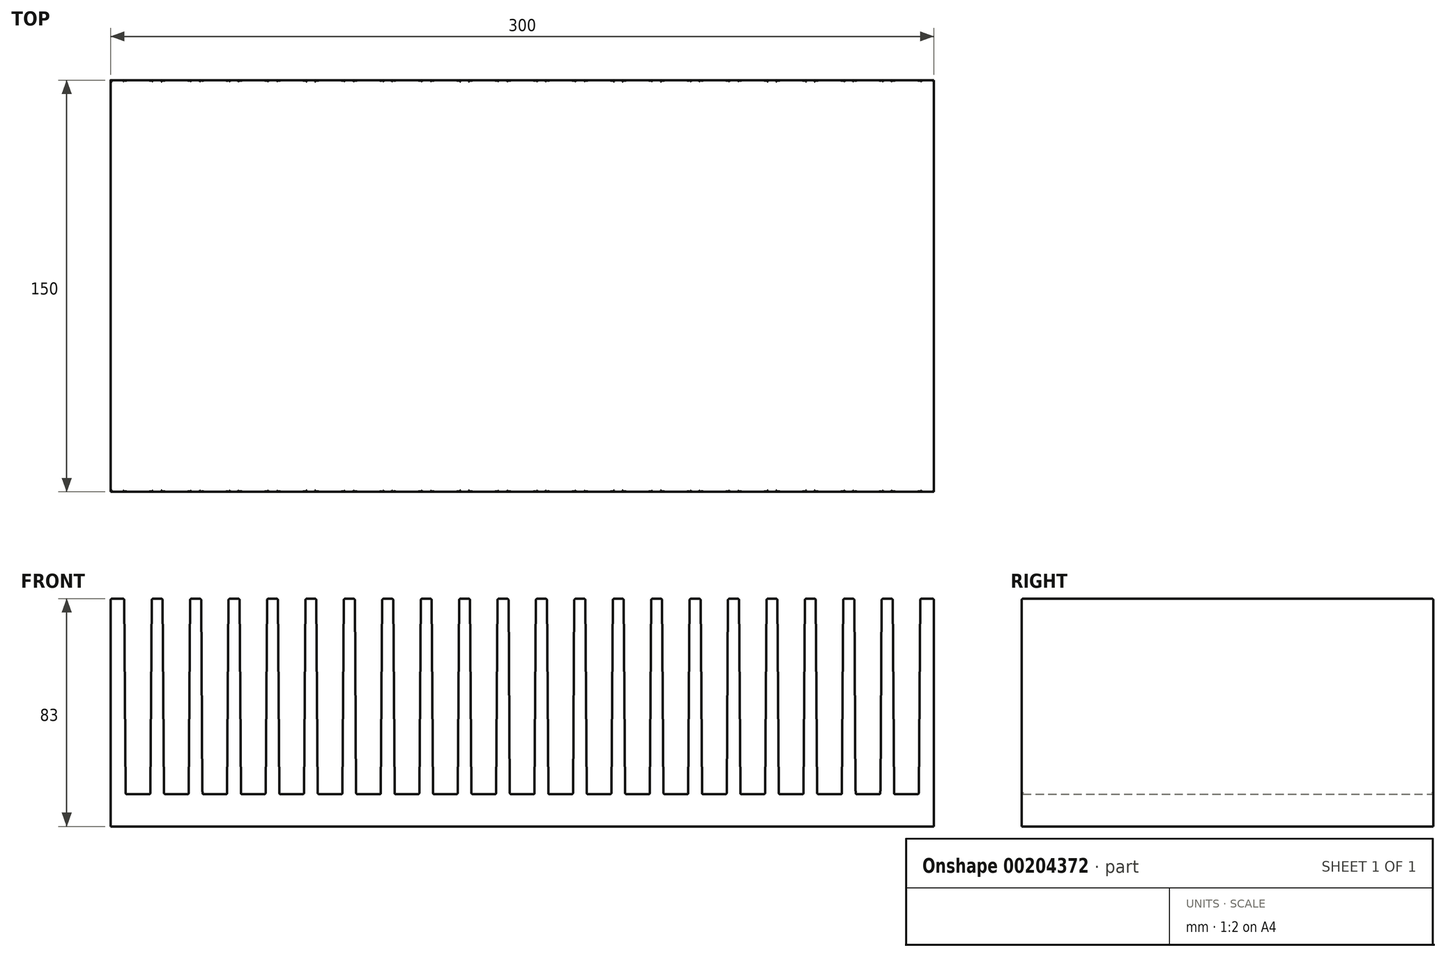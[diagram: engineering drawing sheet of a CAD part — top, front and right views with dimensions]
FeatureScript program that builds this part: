
annotation { "Feature Type Name" : "Feature", "Feature Type Description" : "" }
export const myFeature = defineFeature(function(context is Context, id is Id, definition is map)
    precondition{}
    {
        {
            var Q0;
            Q0=qCreatedBy(makeId("Front.planeOp"),FACE);
            var sketch = newSketch(context, id + "F0", { "sketchPlane" : qUnion([Q0])});
            skLineSegment(sketch, "E0", {"start": v(0, 0) * mm, "end": v(4.5, 0) * mm});
            skLineSegment(sketch, "E1", {"start": v(0, 0) * mm, "end": v(-4.5, 0) * mm});
            skLineSegment(sketch, "E2", {"start": v(0, 0) * mm, "end": v(0, 71.26) * mm, "construction": true});
            skLineSegment(sketch, "E3", {"start": v(-4.5, 0) * mm, "end": v(-5, 71.3) * mm});
            skLineSegment(sketch, "E4", {"start": v(4.5, 0) * mm, "end": v(5, 71.3) * mm});
            skLineSegment(sketch, "E5", {"start": v(-5, 71.3) * mm, "end": v(-9, 71.3) * mm});
            skLineSegment(sketch, "E6.1.0.0", {"start": v(9.5, 0) * mm, "end": v(9, 71.3) * mm});
            skLineSegment(sketch, "E6.1.0.1", {"start": v(14, 0) * mm, "end": v(9.5, 0) * mm});
            skLineSegment(sketch, "E6.1.0.2", {"start": v(14, 0) * mm, "end": v(18.5, 0) * mm});
            skLineSegment(sketch, "E6.1.0.3", {"start": v(18.5, 0) * mm, "end": v(19, 71.3) * mm});
            skLineSegment(sketch, "E6.1.0.4", {"start": v(9, 71.3) * mm, "end": v(5, 71.3) * mm});
            skLineSegment(sketch, "E6.2.0.0", {"start": v(23.5, 0) * mm, "end": v(23, 71.3) * mm});
            skLineSegment(sketch, "E6.2.0.1", {"start": v(28, 0) * mm, "end": v(23.5, 0) * mm});
            skLineSegment(sketch, "E6.2.0.2", {"start": v(28, 0) * mm, "end": v(32.5, 0) * mm});
            skLineSegment(sketch, "E6.2.0.3", {"start": v(32.5, 0) * mm, "end": v(33, 71.3) * mm});
            skLineSegment(sketch, "E6.2.0.4", {"start": v(23, 71.3) * mm, "end": v(19, 71.3) * mm});
            skLineSegment(sketch, "E6.3.0.0", {"start": v(37.5, 0) * mm, "end": v(37, 71.3) * mm});
            skLineSegment(sketch, "E6.3.0.1", {"start": v(42, 0) * mm, "end": v(37.5, 0) * mm});
            skLineSegment(sketch, "E6.3.0.2", {"start": v(42, 0) * mm, "end": v(46.5, 0) * mm});
            skLineSegment(sketch, "E6.3.0.3", {"start": v(46.5, 0) * mm, "end": v(47, 71.3) * mm});
            skLineSegment(sketch, "E6.3.0.4", {"start": v(37, 71.3) * mm, "end": v(33, 71.3) * mm});
            skLineSegment(sketch, "E6.4.0.0", {"start": v(51.5, 0) * mm, "end": v(51, 71.3) * mm});
            skLineSegment(sketch, "E6.4.0.1", {"start": v(56, 0) * mm, "end": v(51.5, 0) * mm});
            skLineSegment(sketch, "E6.4.0.2", {"start": v(56, 0) * mm, "end": v(60.5, 0) * mm});
            skLineSegment(sketch, "E6.4.0.3", {"start": v(60.5, 0) * mm, "end": v(61, 71.3) * mm});
            skLineSegment(sketch, "E6.4.0.4", {"start": v(51, 71.3) * mm, "end": v(47, 71.3) * mm});
            skLineSegment(sketch, "E6.5.0.0", {"start": v(65.5, 0) * mm, "end": v(65, 71.3) * mm});
            skLineSegment(sketch, "E6.5.0.1", {"start": v(70, 0) * mm, "end": v(65.5, 0) * mm});
            skLineSegment(sketch, "E6.5.0.2", {"start": v(70, 0) * mm, "end": v(74.5, 0) * mm});
            skLineSegment(sketch, "E6.5.0.3", {"start": v(74.5, 0) * mm, "end": v(75, 71.3) * mm});
            skLineSegment(sketch, "E6.5.0.4", {"start": v(65, 71.3) * mm, "end": v(61, 71.3) * mm});
            skLineSegment(sketch, "E6.6.0.0", {"start": v(79.5, 0) * mm, "end": v(79, 71.3) * mm});
            skLineSegment(sketch, "E6.6.0.1", {"start": v(84, 0) * mm, "end": v(79.5, 0) * mm});
            skLineSegment(sketch, "E6.6.0.2", {"start": v(84, 0) * mm, "end": v(88.5, 0) * mm});
            skLineSegment(sketch, "E6.6.0.3", {"start": v(88.5, 0) * mm, "end": v(89, 71.3) * mm});
            skLineSegment(sketch, "E6.6.0.4", {"start": v(79, 71.3) * mm, "end": v(75, 71.3) * mm});
            skLineSegment(sketch, "E6.7.0.0", {"start": v(93.5, 0) * mm, "end": v(93, 71.3) * mm});
            skLineSegment(sketch, "E6.7.0.1", {"start": v(98, 0) * mm, "end": v(93.5, 0) * mm});
            skLineSegment(sketch, "E6.7.0.2", {"start": v(98, 0) * mm, "end": v(102.5, 0) * mm});
            skLineSegment(sketch, "E6.7.0.3", {"start": v(102.5, 0) * mm, "end": v(103, 71.3) * mm});
            skLineSegment(sketch, "E6.7.0.4", {"start": v(93, 71.3) * mm, "end": v(89, 71.3) * mm});
            skLineSegment(sketch, "E6.8.0.0", {"start": v(107.5, 0) * mm, "end": v(107, 71.3) * mm});
            skLineSegment(sketch, "E6.8.0.1", {"start": v(112, 0) * mm, "end": v(107.5, 0) * mm});
            skLineSegment(sketch, "E6.8.0.2", {"start": v(112, 0) * mm, "end": v(116.5, 0) * mm});
            skLineSegment(sketch, "E6.8.0.3", {"start": v(116.5, 0) * mm, "end": v(117, 71.3) * mm});
            skLineSegment(sketch, "E6.8.0.4", {"start": v(107, 71.3) * mm, "end": v(103, 71.3) * mm});
            skLineSegment(sketch, "E6.9.0.0", {"start": v(121.5, 0) * mm, "end": v(121, 71.3) * mm});
            skLineSegment(sketch, "E6.9.0.1", {"start": v(126, 0) * mm, "end": v(121.5, 0) * mm});
            skLineSegment(sketch, "E6.9.0.2", {"start": v(126, 0) * mm, "end": v(130.5, 0) * mm});
            skLineSegment(sketch, "E6.9.0.3", {"start": v(130.5, 0) * mm, "end": v(131, 71.3) * mm});
            skLineSegment(sketch, "E6.9.0.4", {"start": v(121, 71.3) * mm, "end": v(117, 71.3) * mm});
            skLineSegment(sketch, "E6.10.0.0", {"start": v(135.5, 0) * mm, "end": v(135, 71.3) * mm});
            skLineSegment(sketch, "E6.10.0.1", {"start": v(140, 0) * mm, "end": v(135.5, 0) * mm});
            skLineSegment(sketch, "E6.10.0.2", {"start": v(140, 0) * mm, "end": v(144.5, 0) * mm});
            skLineSegment(sketch, "E6.10.0.3", {"start": v(144.5, 0) * mm, "end": v(145, 71.3) * mm});
            skLineSegment(sketch, "E6.10.0.4", {"start": v(135, 71.3) * mm, "end": v(131, 71.3) * mm});
            skLineSegment(sketch, "E6.11.0.0", {"start": v(149.5, 0) * mm, "end": v(149, 71.3) * mm});
            skLineSegment(sketch, "E6.11.0.1", {"start": v(154, 0) * mm, "end": v(149.5, 0) * mm});
            skLineSegment(sketch, "E6.11.0.2", {"start": v(154, 0) * mm, "end": v(158.5, 0) * mm});
            skLineSegment(sketch, "E6.11.0.3", {"start": v(158.5, 0) * mm, "end": v(159, 71.3) * mm});
            skLineSegment(sketch, "E6.11.0.4", {"start": v(149, 71.3) * mm, "end": v(145, 71.3) * mm});
            skLineSegment(sketch, "E6.12.0.0", {"start": v(163.5, 0) * mm, "end": v(163, 71.3) * mm});
            skLineSegment(sketch, "E6.12.0.1", {"start": v(168, 0) * mm, "end": v(163.5, 0) * mm});
            skLineSegment(sketch, "E6.12.0.2", {"start": v(168, 0) * mm, "end": v(172.5, 0) * mm});
            skLineSegment(sketch, "E6.12.0.3", {"start": v(172.5, 0) * mm, "end": v(173, 71.3) * mm});
            skLineSegment(sketch, "E6.12.0.4", {"start": v(163, 71.3) * mm, "end": v(159, 71.3) * mm});
            skLineSegment(sketch, "E6.13.0.0", {"start": v(177.5, 0) * mm, "end": v(177, 71.3) * mm});
            skLineSegment(sketch, "E6.13.0.1", {"start": v(182, 0) * mm, "end": v(177.5, 0) * mm});
            skLineSegment(sketch, "E6.13.0.2", {"start": v(182, 0) * mm, "end": v(186.5, 0) * mm});
            skLineSegment(sketch, "E6.13.0.3", {"start": v(186.5, 0) * mm, "end": v(187, 71.3) * mm});
            skLineSegment(sketch, "E6.13.0.4", {"start": v(177, 71.3) * mm, "end": v(173, 71.3) * mm});
            skLineSegment(sketch, "E6.14.0.0", {"start": v(191.5, 0) * mm, "end": v(191, 71.3) * mm});
            skLineSegment(sketch, "E6.14.0.1", {"start": v(196, 0) * mm, "end": v(191.5, 0) * mm});
            skLineSegment(sketch, "E6.14.0.2", {"start": v(196, 0) * mm, "end": v(200.5, 0) * mm});
            skLineSegment(sketch, "E6.14.0.3", {"start": v(200.5, 0) * mm, "end": v(201, 71.3) * mm});
            skLineSegment(sketch, "E6.14.0.4", {"start": v(191, 71.3) * mm, "end": v(187, 71.3) * mm});
            skLineSegment(sketch, "E6.15.0.0", {"start": v(205.5, 0) * mm, "end": v(205, 71.3) * mm});
            skLineSegment(sketch, "E6.15.0.1", {"start": v(210, 0) * mm, "end": v(205.5, 0) * mm});
            skLineSegment(sketch, "E6.15.0.2", {"start": v(210, 0) * mm, "end": v(214.5, 0) * mm});
            skLineSegment(sketch, "E6.15.0.3", {"start": v(214.5, 0) * mm, "end": v(215, 71.3) * mm});
            skLineSegment(sketch, "E6.15.0.4", {"start": v(205, 71.3) * mm, "end": v(201, 71.3) * mm});
            skLineSegment(sketch, "E6.16.0.0", {"start": v(219.5, 0) * mm, "end": v(219, 71.3) * mm});
            skLineSegment(sketch, "E6.16.0.1", {"start": v(224, 0) * mm, "end": v(219.5, 0) * mm});
            skLineSegment(sketch, "E6.16.0.2", {"start": v(224, 0) * mm, "end": v(228.5, 0) * mm});
            skLineSegment(sketch, "E6.16.0.3", {"start": v(228.5, 0) * mm, "end": v(229, 71.3) * mm});
            skLineSegment(sketch, "E6.16.0.4", {"start": v(219, 71.3) * mm, "end": v(215, 71.3) * mm});
            skLineSegment(sketch, "E6.17.0.0", {"start": v(233.5, 0) * mm, "end": v(233, 71.3) * mm});
            skLineSegment(sketch, "E6.17.0.1", {"start": v(238, 0) * mm, "end": v(233.5, 0) * mm});
            skLineSegment(sketch, "E6.17.0.2", {"start": v(238, 0) * mm, "end": v(242.5, 0) * mm});
            skLineSegment(sketch, "E6.17.0.3", {"start": v(242.5, 0) * mm, "end": v(243, 71.3) * mm});
            skLineSegment(sketch, "E6.17.0.4", {"start": v(233, 71.3) * mm, "end": v(229, 71.3) * mm});
            skLineSegment(sketch, "E6.18.0.0", {"start": v(247.5, 0) * mm, "end": v(247, 71.3) * mm});
            skLineSegment(sketch, "E6.18.0.1", {"start": v(252, 0) * mm, "end": v(247.5, 0) * mm});
            skLineSegment(sketch, "E6.18.0.2", {"start": v(252, 0) * mm, "end": v(256.5, 0) * mm});
            skLineSegment(sketch, "E6.18.0.3", {"start": v(256.5, 0) * mm, "end": v(257, 71.3) * mm});
            skLineSegment(sketch, "E6.18.0.4", {"start": v(247, 71.3) * mm, "end": v(243, 71.3) * mm});
            skLineSegment(sketch, "E6.19.0.0", {"start": v(261.5, 0) * mm, "end": v(261, 71.3) * mm});
            skLineSegment(sketch, "E6.19.0.1", {"start": v(266, 0) * mm, "end": v(261.5, 0) * mm});
            skLineSegment(sketch, "E6.19.0.2", {"start": v(266, 0) * mm, "end": v(270.5, 0) * mm});
            skLineSegment(sketch, "E6.19.0.3", {"start": v(270.5, 0) * mm, "end": v(271, 71.3) * mm});
            skLineSegment(sketch, "E6.19.0.4", {"start": v(261, 71.3) * mm, "end": v(257, 71.3) * mm});
            skLineSegment(sketch, "E6.direction1", {"start": v(-4.5, 0) * mm, "end": v(9.5, 0) * mm, "construction": true});
            skLineSegment(sketch, "E7", {"start": v(-9, 71.3) * mm, "end": v(-10, 71.3) * mm});
            skLineSegment(sketch, "E8", {"start": v(-10, 71.3) * mm, "end": v(-10, -11.7) * mm});
            skLineSegment(sketch, "E9", {"start": v(-10, -11.7) * mm, "end": v(290, -11.7) * mm});
            skLineSegment(sketch, "E10.0.20.0", {"start": v(275.5, 0) * mm, "end": v(275, 71.3) * mm});
            skLineSegment(sketch, "E10.3.20.0", {"start": v(280, 0) * mm, "end": v(275.5, 0) * mm});
            skLineSegment(sketch, "E10.6.20.0", {"start": v(280, 0) * mm, "end": v(284.5, 0) * mm});
            skLineSegment(sketch, "E10.9.20.0", {"start": v(284.5, 0) * mm, "end": v(285, 71.3) * mm});
            skLineSegment(sketch, "E10.12.20.0", {"start": v(275, 71.3) * mm, "end": v(271, 71.3) * mm});
            skLineSegment(sketch, "E11", {"start": v(285, 71.3) * mm, "end": v(290, 71.3) * mm});
            skLineSegment(sketch, "E12", {"start": v(290, 71.3) * mm, "end": v(290, -11.7) * mm});
            skSolve(sketch);
        }
        {
            var Q0;
            Q0 = qSketchRegion(id + "F0", true);
            extrude(context, id + "F1", {"entities" : qUnion([Q0]), "depth" : 150 * mm});
        }
        {
            var Q0;
            Q0=makeQuery(id+"F1.opExtrude","SWEPT_FACE",FACE,{"disambiguationData":[OSD([sQuery(id+"F0.wireOp",EDGE,"E5"),sQuery(id+"F0.wireOp",EDGE,"E7")])]});
            var Q1;
            Q1=makeQuery(id+"F1.opExtrude","SWEPT_FACE",FACE,{"disambiguationData":[OSD([sQuery(id+"F0.wireOp",EDGE,"E6.1.0.4")])]});
            var Q2;
            Q2=makeQuery(id+"F1.opExtrude","SWEPT_FACE",FACE,{"disambiguationData":[OSD([sQuery(id+"F0.wireOp",EDGE,"E6.2.0.4")])]});
            var Q3;
            Q3=makeQuery(id+"F1.opExtrude","SWEPT_FACE",FACE,{"disambiguationData":[OSD([sQuery(id+"F0.wireOp",EDGE,"E6.3.0.4")])]});
            var Q4;
            Q4=makeQuery(id+"F1.opExtrude","SWEPT_FACE",FACE,{"disambiguationData":[OSD([sQuery(id+"F0.wireOp",EDGE,"E6.4.0.4")])]});
            var Q5;
            Q5=makeQuery(id+"F1.opExtrude","SWEPT_FACE",FACE,{"disambiguationData":[OSD([sQuery(id+"F0.wireOp",EDGE,"E6.5.0.4")])]});
            var Q6;
            Q6=makeQuery(id+"F1.opExtrude","SWEPT_FACE",FACE,{"disambiguationData":[OSD([sQuery(id+"F0.wireOp",EDGE,"E6.6.0.4")])]});
            var Q7;
            Q7=makeQuery(id+"F1.opExtrude","SWEPT_FACE",FACE,{"disambiguationData":[OSD([sQuery(id+"F0.wireOp",EDGE,"E6.7.0.4")])]});
            var Q8;
            Q8=makeQuery(id+"F1.opExtrude","SWEPT_FACE",FACE,{"disambiguationData":[OSD([sQuery(id+"F0.wireOp",EDGE,"E6.8.0.4")])]});
            var Q9;
            Q9=makeQuery(id+"F1.opExtrude","SWEPT_FACE",FACE,{"disambiguationData":[OSD([sQuery(id+"F0.wireOp",EDGE,"E6.9.0.4")])]});
            var Q10;
            Q10=makeQuery(id+"F1.opExtrude","SWEPT_FACE",FACE,{"disambiguationData":[OSD([sQuery(id+"F0.wireOp",EDGE,"E6.10.0.4")])]});
            var Q11;
            Q11=makeQuery(id+"F1.opExtrude","SWEPT_FACE",FACE,{"disambiguationData":[OSD([sQuery(id+"F0.wireOp",EDGE,"E6.11.0.4")])]});
            var Q12;
            Q12=makeQuery(id+"F1.opExtrude","SWEPT_FACE",FACE,{"disambiguationData":[OSD([sQuery(id+"F0.wireOp",EDGE,"E6.12.0.4")])]});
            var Q13;
            Q13=makeQuery(id+"F1.opExtrude","SWEPT_FACE",FACE,{"disambiguationData":[OSD([sQuery(id+"F0.wireOp",EDGE,"E6.13.0.4")])]});
            var Q14;
            Q14=makeQuery(id+"F1.opExtrude","SWEPT_FACE",FACE,{"disambiguationData":[OSD([sQuery(id+"F0.wireOp",EDGE,"E6.14.0.4")])]});
            var Q15;
            Q15=makeQuery(id+"F1.opExtrude","SWEPT_FACE",FACE,{"disambiguationData":[OSD([sQuery(id+"F0.wireOp",EDGE,"E6.15.0.4")])]});
            var Q16;
            Q16=makeQuery(id+"F1.opExtrude","SWEPT_FACE",FACE,{"disambiguationData":[OSD([sQuery(id+"F0.wireOp",EDGE,"E6.16.0.4")])]});
            var Q17;
            Q17=makeQuery(id+"F1.opExtrude","SWEPT_FACE",FACE,{"disambiguationData":[OSD([sQuery(id+"F0.wireOp",EDGE,"E6.17.0.4")])]});
            var Q18;
            Q18=makeQuery(id+"F1.opExtrude","SWEPT_FACE",FACE,{"disambiguationData":[OSD([sQuery(id+"F0.wireOp",EDGE,"E6.18.0.4")])]});
            var Q19;
            Q19=makeQuery(id+"F1.opExtrude","SWEPT_FACE",FACE,{"disambiguationData":[OSD([sQuery(id+"F0.wireOp",EDGE,"E6.19.0.4")])]});
            var Q20;
            Q20=makeQuery(id+"F1.opExtrude","SWEPT_FACE",FACE,{"disambiguationData":[OSD([sQuery(id+"F0.wireOp",EDGE,"E10.12.20.0")])]});
            var Q21;
            Q21=makeQuery(id+"F1.opExtrude","SWEPT_FACE",FACE,{"disambiguationData":[OSD([sQuery(id+"F0.wireOp",EDGE,"E11")])]});
            var Q22;
            Q22=makeQuery(id+"F1.opExtrude","SWEPT_FACE",FACE,{"disambiguationData":[OSD([sQuery(id+"F0.wireOp",EDGE,"E10.3.20.0"),sQuery(id+"F0.wireOp",EDGE,"E10.6.20.0")])]});
            var Q23;
            Q23=makeQuery(id+"F1.opExtrude","SWEPT_FACE",FACE,{"disambiguationData":[OSD([sQuery(id+"F0.wireOp",EDGE,"E6.19.0.1"),sQuery(id+"F0.wireOp",EDGE,"E6.19.0.2")])]});
            var Q24;
            Q24=makeQuery(id+"F1.opExtrude","SWEPT_FACE",FACE,{"disambiguationData":[OSD([sQuery(id+"F0.wireOp",EDGE,"E6.18.0.1"),sQuery(id+"F0.wireOp",EDGE,"E6.18.0.2")])]});
            var Q25;
            Q25=makeQuery(id+"F1.opExtrude","SWEPT_FACE",FACE,{"disambiguationData":[OSD([sQuery(id+"F0.wireOp",EDGE,"E6.17.0.1"),sQuery(id+"F0.wireOp",EDGE,"E6.17.0.2")])]});
            var Q26;
            Q26=makeQuery(id+"F1.opExtrude","SWEPT_FACE",FACE,{"disambiguationData":[OSD([sQuery(id+"F0.wireOp",EDGE,"E6.16.0.1"),sQuery(id+"F0.wireOp",EDGE,"E6.16.0.2")])]});
            var Q27;
            Q27=makeQuery(id+"F1.opExtrude","SWEPT_FACE",FACE,{"disambiguationData":[OSD([sQuery(id+"F0.wireOp",EDGE,"E6.15.0.1"),sQuery(id+"F0.wireOp",EDGE,"E6.15.0.2")])]});
            var Q28;
            Q28=makeQuery(id+"F1.opExtrude","SWEPT_FACE",FACE,{"disambiguationData":[OSD([sQuery(id+"F0.wireOp",EDGE,"E6.14.0.1"),sQuery(id+"F0.wireOp",EDGE,"E6.14.0.2")])]});
            var Q29;
            Q29=makeQuery(id+"F1.opExtrude","SWEPT_FACE",FACE,{"disambiguationData":[OSD([sQuery(id+"F0.wireOp",EDGE,"E6.13.0.1"),sQuery(id+"F0.wireOp",EDGE,"E6.13.0.2")])]});
            var Q30;
            Q30=makeQuery(id+"F1.opExtrude","SWEPT_FACE",FACE,{"disambiguationData":[OSD([sQuery(id+"F0.wireOp",EDGE,"E6.12.0.1"),sQuery(id+"F0.wireOp",EDGE,"E6.12.0.2")])]});
            var Q31;
            Q31=makeQuery(id+"F1.opExtrude","SWEPT_FACE",FACE,{"disambiguationData":[OSD([sQuery(id+"F0.wireOp",EDGE,"E6.11.0.1"),sQuery(id+"F0.wireOp",EDGE,"E6.11.0.2")])]});
            var Q32;
            Q32=makeQuery(id+"F1.opExtrude","SWEPT_FACE",FACE,{"disambiguationData":[OSD([sQuery(id+"F0.wireOp",EDGE,"E6.10.0.1"),sQuery(id+"F0.wireOp",EDGE,"E6.10.0.2")])]});
            var Q33;
            Q33=makeQuery(id+"F1.opExtrude","SWEPT_FACE",FACE,{"disambiguationData":[OSD([sQuery(id+"F0.wireOp",EDGE,"E6.9.0.1"),sQuery(id+"F0.wireOp",EDGE,"E6.9.0.2")])]});
            var Q34;
            Q34=makeQuery(id+"F1.opExtrude","SWEPT_FACE",FACE,{"disambiguationData":[OSD([sQuery(id+"F0.wireOp",EDGE,"E6.8.0.1"),sQuery(id+"F0.wireOp",EDGE,"E6.8.0.2")])]});
            var Q35;
            Q35=makeQuery(id+"F1.opExtrude","SWEPT_FACE",FACE,{"disambiguationData":[OSD([sQuery(id+"F0.wireOp",EDGE,"E6.7.0.1"),sQuery(id+"F0.wireOp",EDGE,"E6.7.0.2")])]});
            var Q36;
            Q36=makeQuery(id+"F1.opExtrude","SWEPT_FACE",FACE,{"disambiguationData":[OSD([sQuery(id+"F0.wireOp",EDGE,"E6.6.0.1"),sQuery(id+"F0.wireOp",EDGE,"E6.6.0.2")])]});
            var Q37;
            Q37=makeQuery(id+"F1.opExtrude","SWEPT_FACE",FACE,{"disambiguationData":[OSD([sQuery(id+"F0.wireOp",EDGE,"E6.5.0.1"),sQuery(id+"F0.wireOp",EDGE,"E6.5.0.2")])]});
            var Q38;
            Q38=makeQuery(id+"F1.opExtrude","SWEPT_FACE",FACE,{"disambiguationData":[OSD([sQuery(id+"F0.wireOp",EDGE,"E6.4.0.1"),sQuery(id+"F0.wireOp",EDGE,"E6.4.0.2")])]});
            var Q39;
            Q39=makeQuery(id+"F1.opExtrude","SWEPT_FACE",FACE,{"disambiguationData":[OSD([sQuery(id+"F0.wireOp",EDGE,"E6.3.0.1"),sQuery(id+"F0.wireOp",EDGE,"E6.3.0.2")])]});
            var Q40;
            Q40=makeQuery(id+"F1.opExtrude","SWEPT_FACE",FACE,{"disambiguationData":[OSD([sQuery(id+"F0.wireOp",EDGE,"E6.2.0.1"),sQuery(id+"F0.wireOp",EDGE,"E6.2.0.2")])]});
            var Q41;
            Q41=makeQuery(id+"F1.opExtrude","SWEPT_FACE",FACE,{"disambiguationData":[OSD([sQuery(id+"F0.wireOp",EDGE,"E6.1.0.1"),sQuery(id+"F0.wireOp",EDGE,"E6.1.0.2")])]});
            var Q42;
            Q42=makeQuery(id+"F1.opExtrude","SWEPT_FACE",FACE,{"disambiguationData":[OSD([sQuery(id+"F0.wireOp",EDGE,"E0"),sQuery(id+"F0.wireOp",EDGE,"E1")])]});
            fillet(context, id + "F2", {"entities" : qUnion([Q0, Q1, Q2, Q3, Q4, Q5, Q6, Q7, Q8, Q9, Q10, Q11, Q12, Q13, Q14, Q15, Q16, Q17, Q18, Q19, Q20, Q21, Q22, Q23, Q24, Q25, Q26, Q27, Q28, Q29, Q30, Q31, Q32, Q33, Q34, Q35, Q36, Q37, Q38, Q39, Q40, Q41, Q42]), "radius" : 0.5 * mm, "tangentPropagation" : true, "allowEdgeOverflow" : false});
        }
    });
